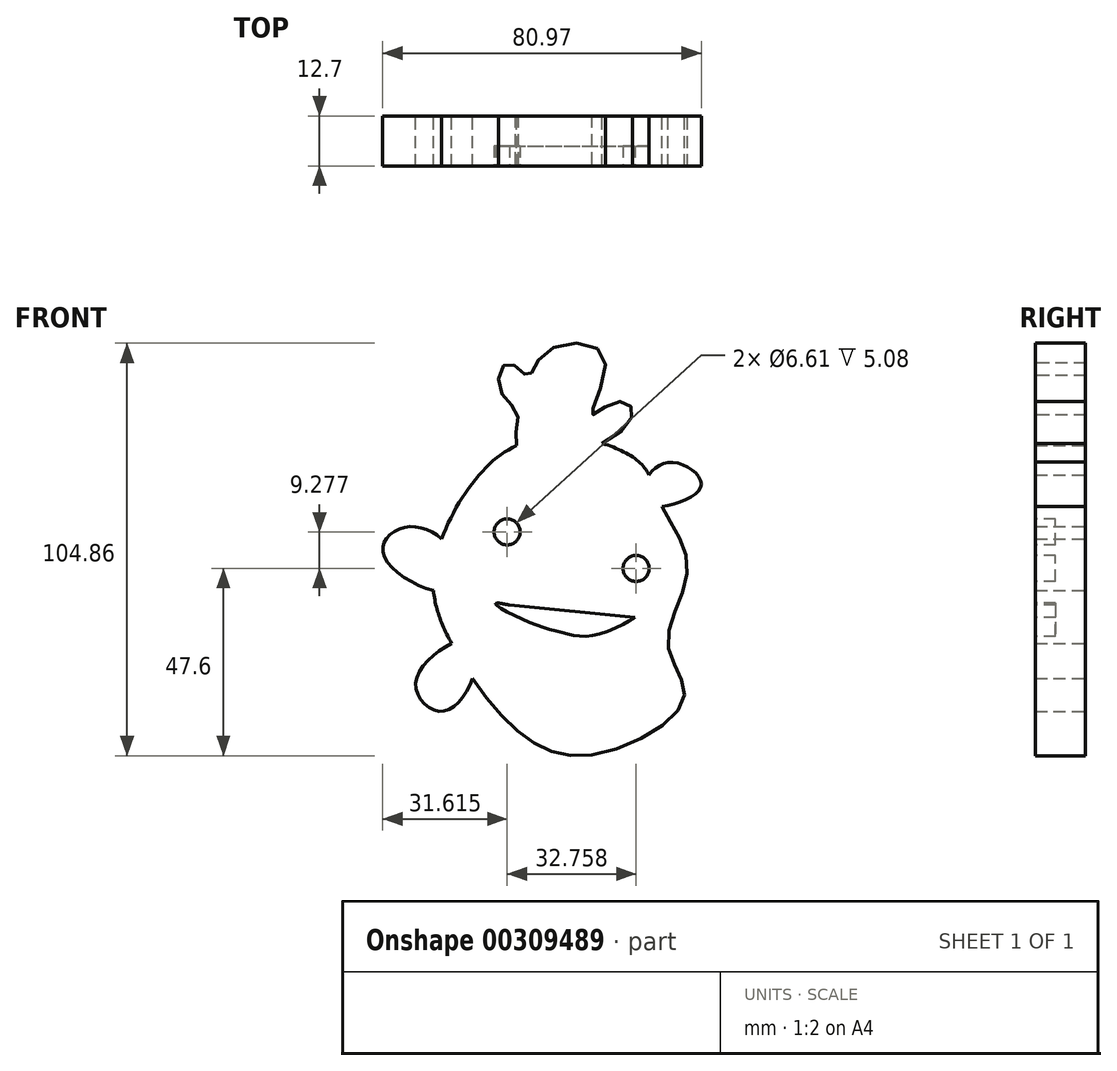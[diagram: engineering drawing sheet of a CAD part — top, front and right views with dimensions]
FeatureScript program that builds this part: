
annotation { "Feature Type Name" : "Feature", "Feature Type Description" : "" }
export const myFeature = defineFeature(function(context is Context, id is Id, definition is map)
    precondition{}
    {
        {
            var Q0;
            Q0=qCreatedBy(makeId("Front.planeOp"),FACE);
            var sketch = newSketch(context, id + "F0", { "sketchPlane" : qUnion([Q0])});
            skPoint(sketch, "E0.center.orphan", {"position": v(0, 33.34) * mm});
            skFitSpline(sketch, "E1", {"points": [v(21.79, 19.04) * mm, v(28.7, 26.96) * mm, v(37.1, 20.87) * mm, v(23.4, 15.74) * mm, v(21.79, 19.04) * mm]});
            skFitSpline(sketch, "E2", {"points": [v(-26.3, 4.55) * mm, v(-38.27, 10.44) * mm, v(-43.48, 3.19) * mm, v(-26.16, -5.65) * mm, v(-26.3, 4.55) * mm]});
            skFitSpline(sketch, "E3", {"points": [v(-22.35, -17.99) * mm, v(-35.37, -28.7) * mm, v(-28.12, -36.24) * mm, v(-19.56, -22.54) * mm, v(-22.35, -17.99) * mm]});
            skPoint(sketch, "E4.3.internal.orphan", {"position": v(0, 41.74) * mm});
            skFitSpline(sketch, "E5", {"points": [v(-9.67, 31.04) * mm, v(-9.57, 39.14) * mm, v(-14.2, 45.8) * mm, v(-11.89, 52.18) * mm, v(-6.96, 49) * mm, v(-2.6, 54.79) * mm, v(12.47, 53.92) * mm, v(9.28, 39.14) * mm, v(15.36, 42.32) * mm, v(19.71, 40) * mm, v(9.94, 30.91) * mm, v(-9.67, 31.04) * mm]});
            skFitSpline(sketch, "E6", {"points": [v(0, 33.34) * mm, v(-17.97, 25.22) * mm, v(-30.73, 0) * mm, v(-26.3, -19.07) * mm, v(-9.67, -41.16) * mm, v(9.86, -47.25) * mm, v(32.76, -33.05) * mm, v(28.7, -19.42) * mm, v(33.63, 0) * mm, v(27.23, 15.79) * mm, v(21.45, 26.96) * mm, v(0, 33.34) * mm]});
            skSolve(sketch);
        }
        {
            var Q0;
            Q0 = qSketchRegion(id + "F0", true);
            extrude(context, id + "F1", {"entities" : qUnion([Q0]), "depth" : 12.7 * mm});
        }
        {
            var Q0;
            Q0=makeQuery(id+"F1.opExtrude","CAP_FACE",FACE,{"disambiguationData":[OSD([sQuery(id+"F0.wireOp",EDGE,"E1"),sQuery(id+"F0.wireOp",EDGE,"E2"),sQuery(id+"F0.wireOp",EDGE,"E3"),sQuery(id+"F0.wireOp",EDGE,"E5"),sQuery(id+"F0.wireOp",EDGE,"E6"),sQuery(id+"F0.wireOp",EDGE,"E6"),sQuery(id+"F0.wireOp",EDGE,"E6")])],"isStart":false});
            var sketch = newSketch(context, id + "F2", { "sketchPlane" : qUnion([Q0])});
            skCircle(sketch, "E7", {"center": v(-12.18, 9.28) * mm, "radius": 3.3 * mm});
            skCircle(sketch, "E8", {"center": v(20.58, 0) * mm, "radius": 3.3 * mm});
            skLineSegment(sketch, "E9", {"start": v(-15.07, -8.99) * mm, "end": v(20.3, -12.47) * mm});
            skPoint(sketch, "E10.6.internal.snap0", {"position": v(2.6, -10.73) * mm});
            skFitSpline(sketch, "E10", {"points": [v(-15.07, -8.99) * mm, v(-7.25, -13.34) * mm, v(2.6, -16.52) * mm, v(11.89, -16.52) * mm, v(20.3, -12.47) * mm, v(10.73, -15.94) * mm, v(-7.25, -10.73) * mm, v(-15.07, -8.99) * mm]});
            skSolve(sketch);
        }
        {
            var Q0;
            Q0 = qSketchRegion(id + "F2", true);
            extrude(context, id + "F3", {"entities" : qUnion([Q0]), "operationType" : NewBodyOperationType.REMOVE, "oppositeDirection" : true, "depth" : 5.08 * mm});
        }
    });
